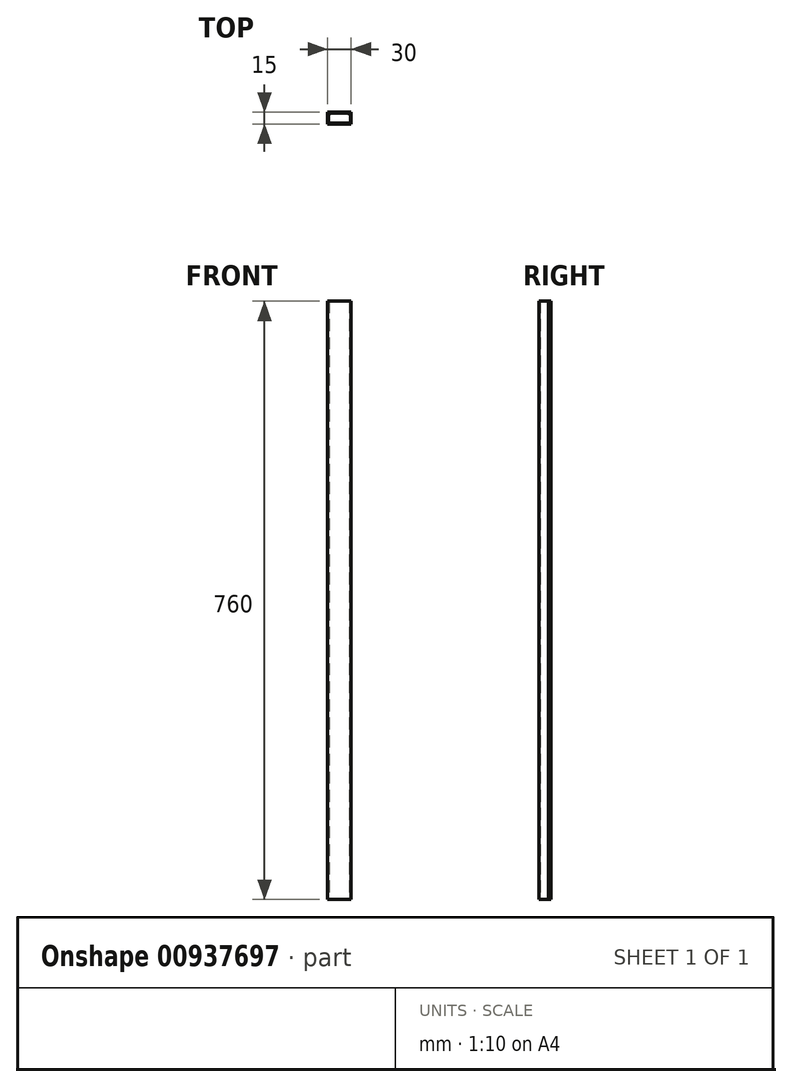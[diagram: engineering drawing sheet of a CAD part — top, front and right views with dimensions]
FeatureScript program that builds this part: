
annotation { "Feature Type Name" : "Feature", "Feature Type Description" : "" }
export const myFeature = defineFeature(function(context is Context, id is Id, definition is map)
    precondition{}
    {
        {
            var Q0;
            Q0=qCreatedBy(makeId("Top.planeOp"),FACE);
            var sketch = newSketch(context, id + "F0", { "sketchPlane" : qUnion([Q0])});
            skLineSegment(sketch, "E0.bottom", {"start": v(-15, 15) * mm, "end": v(15, 15) * mm});
            skLineSegment(sketch, "E0.top", {"start": v(-15, 0) * mm, "end": v(15, 0) * mm});
            skLineSegment(sketch, "E0.left", {"start": v(-15, 15) * mm, "end": v(-15, 0) * mm});
            skLineSegment(sketch, "E0.right", {"start": v(15, 15) * mm, "end": v(15, 0) * mm});
            skLineSegment(sketch, "E1.0", {"start": v(14, 11) * mm, "end": v(14, 1) * mm});
            skLineSegment(sketch, "E1.1", {"start": v(-14, 1) * mm, "end": v(14, 1) * mm});
            skLineSegment(sketch, "E1.2", {"start": v(-14, 11) * mm, "end": v(-14, 1) * mm});
            skLineSegment(sketch, "E2.0", {"start": v(-14, 14) * mm, "end": v(14, 14) * mm});
            skLineSegment(sketch, "E3", {"start": v(-14, 14) * mm, "end": v(-14, 12) * mm});
            skLineSegment(sketch, "E4", {"start": v(-14, 12) * mm, "end": v(-15, 12) * mm});
            skLineSegment(sketch, "E5", {"start": v(14, 14) * mm, "end": v(14, 12) * mm});
            skLineSegment(sketch, "E6", {"start": v(14, 12) * mm, "end": v(15, 12) * mm});
            skLineSegment(sketch, "E7.0", {"start": v(-13, 11) * mm, "end": v(-14, 11) * mm});
            skLineSegment(sketch, "E7.1", {"start": v(-13, 14) * mm, "end": v(-13, 11) * mm});
            skLineSegment(sketch, "E8.0", {"start": v(13, 11) * mm, "end": v(14, 11) * mm});
            skLineSegment(sketch, "E8.1", {"start": v(13, 14) * mm, "end": v(13, 11) * mm});
            skSolve(sketch);
        }
        {
            var Q0;
            {var subQ6=sQuery(id+"F0.wireOp",EDGE,"E0.top");Q0=makeQuery(id+"F0.imprint","IMPRINT",FACE,{"disambiguationData":[TD([[makeQuery(id+"F0.imprint","IMPRINT",EDGE,{"derivedFrom":subQ6}),1.0]])]});}
            extrude(context, id + "F1", {"entities" : qUnion([Q0]), "depth" : 760 * mm, "offsetDistance" : 25 * mm});
        }
        {
            var Q0;
            {var subQ4=sQuery(id+"F0.wireOp",EDGE,"E0.bottom");Q0=makeQuery(id+"F0.imprint","IMPRINT",FACE,{"disambiguationData":[TD([[makeQuery(id+"F0.imprint","IMPRINT",EDGE,{"derivedFrom":subQ4}),-1.0]])]});}
            extrude(context, id + "F2", {"entities" : qUnion([Q0]), "depth" : 760 * mm, "offsetDistance" : 25 * mm});
        }
        {
            var Q0;
            Q0=makeQuery(id+"F1.opExtrude","SWEPT_FACE",FACE,{"disambiguationData":[OSD([sQuery(id+"F0.wireOp",EDGE,"E0.top")])]});
            var sketch = newSketch(context, id + "F3", { "sketchPlane" : qUnion([Q0])});
            skPoint(sketch, "E9", {"position": v(0, 15) * mm});
            skSolve(sketch);
        }
    });
